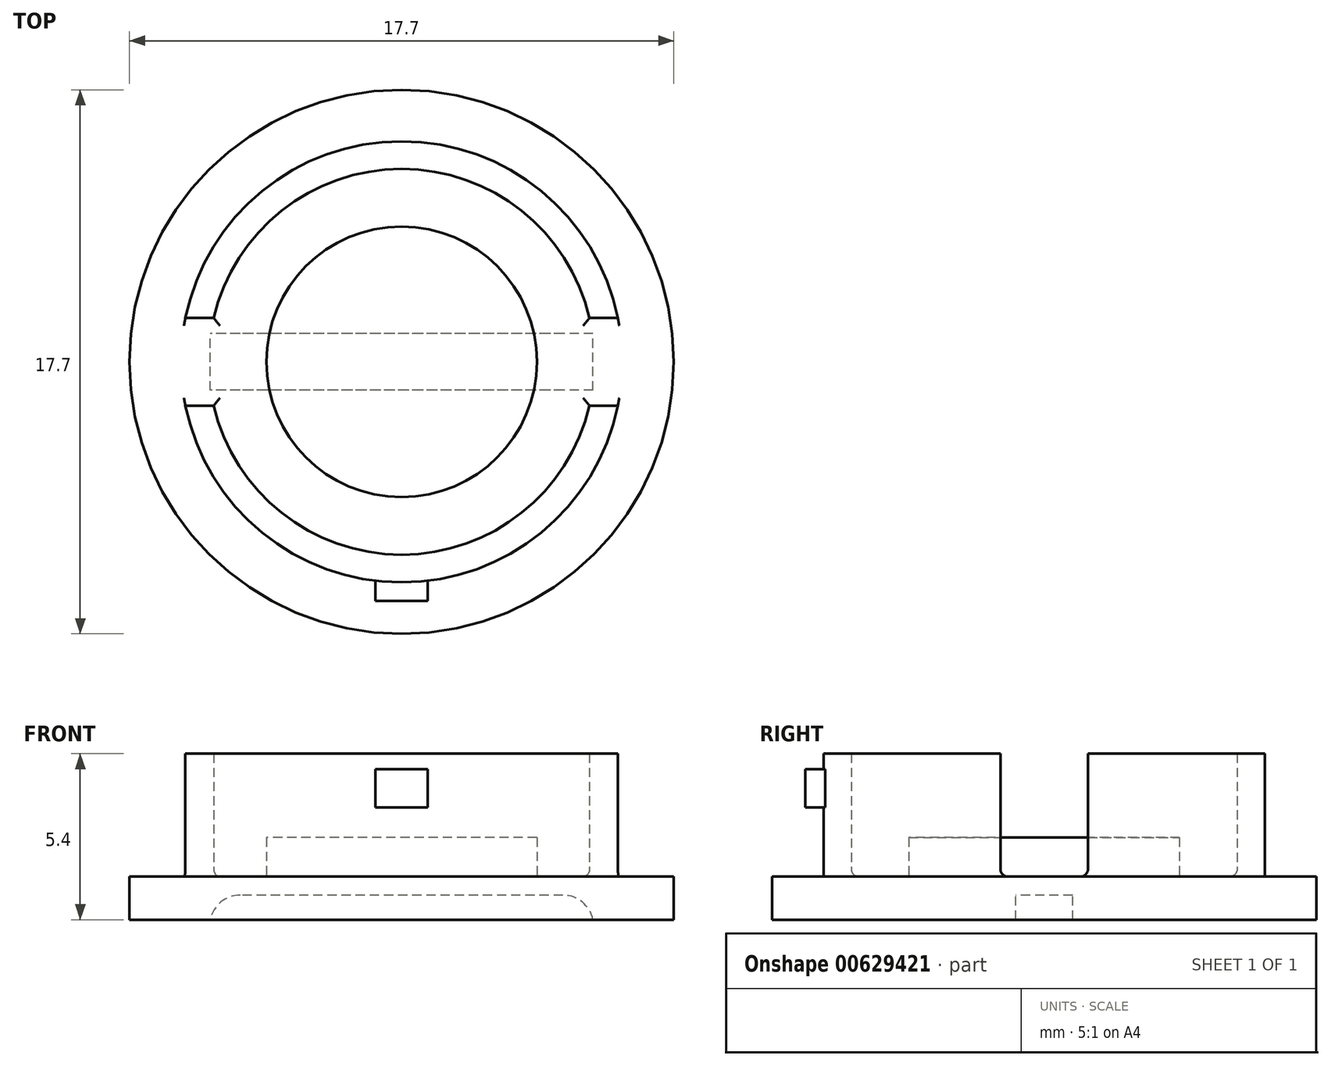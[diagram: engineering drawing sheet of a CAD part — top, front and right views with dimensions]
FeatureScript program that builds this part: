
annotation { "Feature Type Name" : "Feature", "Feature Type Description" : "" }
export const myFeature = defineFeature(function(context is Context, id is Id, definition is map)
    precondition{}
    {
        {
            var Q0;
            Q0=qCreatedBy(makeId("Top.planeOp"),FACE);
            var sketch = newSketch(context, id + "F0", { "sketchPlane" : qUnion([Q0])});
            skCircle(sketch, "E0", {"center": v(0, 0) * mm, "radius": 8.85 * mm});
            skSolve(sketch);
        }
        {
            var Q0;
            Q0=makeQuery(id+"F0.imprint","IMPRINT",FACE,{"disambiguationData":[TD([[makeQuery(id+"F0.imprint","IMPRINT",EDGE,{"derivedFrom":sQuery(id+"F0.wireOp",EDGE,"E0")}),1.0]])]});
            extrude(context, id + "F1", {"entities" : qUnion([Q0]), "depth" : 1.4 * mm, "offsetDistance" : 25.4 * mm});
        }
        {
            var Q0;
            Q0=makeQuery(id+"F1.opExtrude","CAP_FACE",FACE,{"disambiguationData":[OSD([sQuery(id+"F0.wireOp",EDGE,"E0")])],"isStart":false});
            var sketch = newSketch(context, id + "F2", { "sketchPlane" : qUnion([Q0])});
            skCircle(sketch, "E1", {"center": v(0, 0) * mm, "radius": 7.18 * mm});
            skCircle(sketch, "E2.0", {"center": v(0, 0) * mm, "radius": 6.28 * mm});
            skSolve(sketch);
        }
        {
            var Q0;
            Q0=makeQuery(id+"F2.imprint","IMPRINT",FACE,{"disambiguationData":[TD([[makeQuery(id+"F2.imprint","IMPRINT",EDGE,{"derivedFrom":sQuery(id+"F2.wireOp",EDGE,"E1")}),1.0]])]});
            extrude(context, id + "F3", {"entities" : qUnion([Q0]), "operationType" : NewBodyOperationType.ADD, "depth" : 4 * mm, "offsetDistance" : 25 * mm});
        }
        {
            var Q0;
            Q0=qCreatedBy(makeId("Right.planeOp"),FACE);
            cPlane(context, id + "F4", {"entities" : qUnion([Q0]), "cplaneType" : CPlaneType.OFFSET, "offset" : (14.35 / 2) * mm, "width" : 150 * mm, "height" : 150 * mm});
        }
        {
            var Q0;
            Q0=qCreatedBy(id+"F4.planeOp",FACE);
            var sketch = newSketch(context, id + "F5", { "sketchPlane" : qUnion([Q0])});
            skLineSegment(sketch, "E3.bottom", {"start": v(-1.43, 5.4) * mm, "end": v(1.43, 5.4) * mm});
            skLineSegment(sketch, "E3.top", {"start": v(-1.43, 1.4) * mm, "end": v(1.43, 1.4) * mm});
            skLineSegment(sketch, "E3.left", {"start": v(-1.43, 5.4) * mm, "end": v(-1.43, 1.4) * mm});
            skLineSegment(sketch, "E3.right", {"start": v(1.42, 5.4) * mm, "end": v(1.42, 1.4) * mm});
            skLineSegment(sketch, "E4", {"start": v(0, 0) * mm, "end": v(0, 5.4) * mm, "construction": true});
            skSolve(sketch);
        }
        {
            var Q0;
            Q0 = qSketchRegion(id + "F5", true);
            extrude(context, id + "F6", {"entities" : qUnion([Q0]), "operationType" : NewBodyOperationType.REMOVE, "oppositeDirection" : true, "depth" : 25 * mm, "offsetDistance" : 25 * mm});
        }
        {
            var Q0;
            Q0=makeQuery(id+"F3.boolean.opBoolean","SPLIT",FACE,{"disambiguationData":[TD([makeQuery(id+"F3.opExtrude","SWEPT_FACE",FACE,{"disambiguationData":[OSD([sQuery(id+"F2.wireOp",EDGE,"E2.0")])]})])],"derivedFrom":makeQuery(id+"F1.opExtrude","CAP_FACE",FACE,{"disambiguationData":[OSD([sQuery(id+"F0.wireOp",EDGE,"E0")])],"isStart":false})});
            var sketch = newSketch(context, id + "F7", { "sketchPlane" : qUnion([Q0])});
            skCircle(sketch, "E5", {"center": v(0, 0) * mm, "radius": 4.4 * mm});
            skSolve(sketch);
        }
        {
            var Q0;
            Q0 = qSketchRegion(id + "F7", true);
            extrude(context, id + "F8", {"entities" : qUnion([Q0]), "operationType" : NewBodyOperationType.ADD, "depth" : 1.27 * mm, "offsetDistance" : 25 * mm});
        }
        {
            var Q0;
            Q0=qCreatedBy(makeId("Front.planeOp"),FACE);
            cPlane(context, id + "F9", {"entities" : qUnion([Q0]), "cplaneType" : CPlaneType.OFFSET, "offset" : (14.35 / 2) * mm, "width" : 150 * mm, "height" : 150 * mm});
        }
        {
            var Q0;
            Q0=qCreatedBy(id+"F9.planeOp",FACE);
            var sketch = newSketch(context, id + "F10", { "sketchPlane" : qUnion([Q0])});
            skLineSegment(sketch, "E6", {"start": v(0, 0) * mm, "end": v(0, 5.4) * mm, "construction": true});
            skLineSegment(sketch, "E7.bottom", {"start": v(-0.85, 3.65) * mm, "end": v(0.85, 3.65) * mm});
            skLineSegment(sketch, "E7.top", {"start": v(-0.85, 4.9) * mm, "end": v(0.85, 4.9) * mm});
            skLineSegment(sketch, "E7.left", {"start": v(-0.85, 3.65) * mm, "end": v(-0.85, 4.9) * mm});
            skLineSegment(sketch, "E7.right", {"start": v(0.85, 3.65) * mm, "end": v(0.85, 4.9) * mm});
            skSolve(sketch);
        }
        {
            var Q0;
            Q0 = qSketchRegion(id + "F10", true);
            extrude(context, id + "F11", {"entities" : qUnion([Q0]), "operationType" : NewBodyOperationType.ADD, "endBound" : BoundingType.SYMMETRIC, "depth" : 1.2 * mm, "offsetDistance" : 25 * mm});
        }
        {
            var Q0;
            Q0=makeQuery(id+"F1.opExtrude","CAP_FACE",FACE,{"disambiguationData":[OSD([sQuery(id+"F0.wireOp",EDGE,"E0")])],"isStart":true});
            var sketch = newSketch(context, id + "F12", { "sketchPlane" : qUnion([Q0])});
            skLineSegment(sketch, "E8.bottom", {"start": v(6.22, 0.93) * mm, "end": v(-6.22, 0.93) * mm});
            skLineSegment(sketch, "E8.top", {"start": v(6.22, -0.93) * mm, "end": v(-6.22, -0.93) * mm});
            skLineSegment(sketch, "E8.left", {"start": v(6.22, 0.93) * mm, "end": v(6.22, -0.92) * mm});
            skLineSegment(sketch, "E8.right", {"start": v(-6.22, 0.93) * mm, "end": v(-6.22, -0.92) * mm});
            skPoint(sketch, "E8.middle", {"position": v(0, 0) * mm});
            skSolve(sketch);
        }
        {
            var Q0;
            Q0 = qSketchRegion(id + "F12", true);
            extrude(context, id + "F13", {"entities" : qUnion([Q0]), "operationType" : NewBodyOperationType.REMOVE, "oppositeDirection" : true, "depth" : .8 * mm, "offsetDistance" : 25 * mm});
        }
        {
            var Q0;
            Q0=makeQuery(id+"F13.boolean.opBoolean","COPY",EDGE,{"derivedFrom":makeQuery(id+"F13.opExtrude","CAP_EDGE",EDGE,{"disambiguationData":[OSD([sQuery(id+"F12.wireOp",EDGE,"E8.right")])],"isStart":false})});
            var Q1;
            Q1=makeQuery(id+"F13.boolean.opBoolean","COPY",EDGE,{"derivedFrom":makeQuery(id+"F13.opExtrude","CAP_EDGE",EDGE,{"disambiguationData":[OSD([sQuery(id+"F12.wireOp",EDGE,"E8.left")])],"isStart":false})});
            fillet(context, id + "F14", {"entities" : qUnion([Q0, Q1]), "radius" : 1 * mm, "tangentPropagation" : true, "allowEdgeOverflow" : false});
        }
        {
            var Q0;
            {var subQ0=sQuery(id+"F2.wireOp",EDGE,"E2.0");Q0=makeQuery(id+"F6.boolean.opBoolean","SPLIT",EDGE,{"disambiguationData":[TD([makeQuery(id+"F6.opExtrude","SWEPT_FACE",FACE,{"disambiguationData":[OSD([sQuery(id+"F5.wireOp",EDGE,"E3.right")])]})])],"derivedFrom":makeQuery(id+"F3.opExtrude","CAP_EDGE",EDGE,{"disambiguationData":[OSD([subQ0])],"isStart":true})});}
            var Q1;
            Q1=makeQuery(id+"F6.boolean.opBoolean","COPY",EDGE,{"disambiguationData":[OD(1.0)],"derivedFrom":makeQuery(id+"F6.opExtrude","SWEPT_EDGE",EDGE,{"disambiguationData":[OSD([sQuery(id+"F5.wireOp",EDGE,"E3.top"),sQuery(id+"F5.wireOp",EDGE,"E3.right")])]})});
            var Q2;
            {var subQ0=sQuery(id+"F2.wireOp",EDGE,"E1");Q2=makeQuery(id+"F6.boolean.opBoolean","SPLIT",EDGE,{"disambiguationData":[TD([makeQuery(id+"F6.opExtrude","SWEPT_FACE",FACE,{"disambiguationData":[OSD([sQuery(id+"F5.wireOp",EDGE,"E3.right")])]})])],"derivedFrom":makeQuery(id+"F3.opExtrude","CAP_EDGE",EDGE,{"disambiguationData":[OSD([subQ0])],"isStart":true})});}
            var Q3;
            Q3=makeQuery(id+"F6.boolean.opBoolean","COPY",EDGE,{"disambiguationData":[OD(0.0)],"derivedFrom":makeQuery(id+"F6.opExtrude","SWEPT_EDGE",EDGE,{"disambiguationData":[OSD([sQuery(id+"F5.wireOp",EDGE,"E3.top"),sQuery(id+"F5.wireOp",EDGE,"E3.right")])]})});
            var Q4;
            Q4=makeQuery(id+"F8.opExtrude","CAP_EDGE",EDGE,{"disambiguationData":[OSD([sQuery(id+"F7.wireOp",EDGE,"E5")])],"isStart":true});
            var Q5;
            Q5=makeQuery(id+"F6.boolean.opBoolean","COPY",EDGE,{"disambiguationData":[OD(1.0)],"derivedFrom":makeQuery(id+"F6.opExtrude","SWEPT_EDGE",EDGE,{"disambiguationData":[OSD([sQuery(id+"F5.wireOp",EDGE,"E3.top"),sQuery(id+"F5.wireOp",EDGE,"E3.left")])]})});
            var Q6;
            {var subQ0=sQuery(id+"F2.wireOp",EDGE,"E1");Q6=makeQuery(id+"F6.boolean.opBoolean","SPLIT",EDGE,{"disambiguationData":[TD([makeQuery(id+"F6.opExtrude","SWEPT_FACE",FACE,{"disambiguationData":[OSD([sQuery(id+"F5.wireOp",EDGE,"E3.left")])]})])],"derivedFrom":makeQuery(id+"F3.opExtrude","CAP_EDGE",EDGE,{"disambiguationData":[OSD([subQ0])],"isStart":true})});}
            var Q7;
            {var subQ0=sQuery(id+"F2.wireOp",EDGE,"E2.0");Q7=makeQuery(id+"F6.boolean.opBoolean","SPLIT",EDGE,{"disambiguationData":[TD([makeQuery(id+"F6.opExtrude","SWEPT_FACE",FACE,{"disambiguationData":[OSD([sQuery(id+"F5.wireOp",EDGE,"E3.left")])]})])],"derivedFrom":makeQuery(id+"F3.opExtrude","CAP_EDGE",EDGE,{"disambiguationData":[OSD([subQ0])],"isStart":true})});}
            var Q8;
            Q8=makeQuery(id+"F6.boolean.opBoolean","COPY",EDGE,{"disambiguationData":[OD(0.0)],"derivedFrom":makeQuery(id+"F6.opExtrude","SWEPT_EDGE",EDGE,{"disambiguationData":[OSD([sQuery(id+"F5.wireOp",EDGE,"E3.top"),sQuery(id+"F5.wireOp",EDGE,"E3.left")])]})});
            fillet(context, id + "F15", {"entities" : qUnion([Q0, Q1, Q2, Q3, Q4, Q5, Q6, Q7, Q8]), "radius" : .25 * mm, "tangentPropagation" : true, "allowEdgeOverflow" : false});
        }
    });
